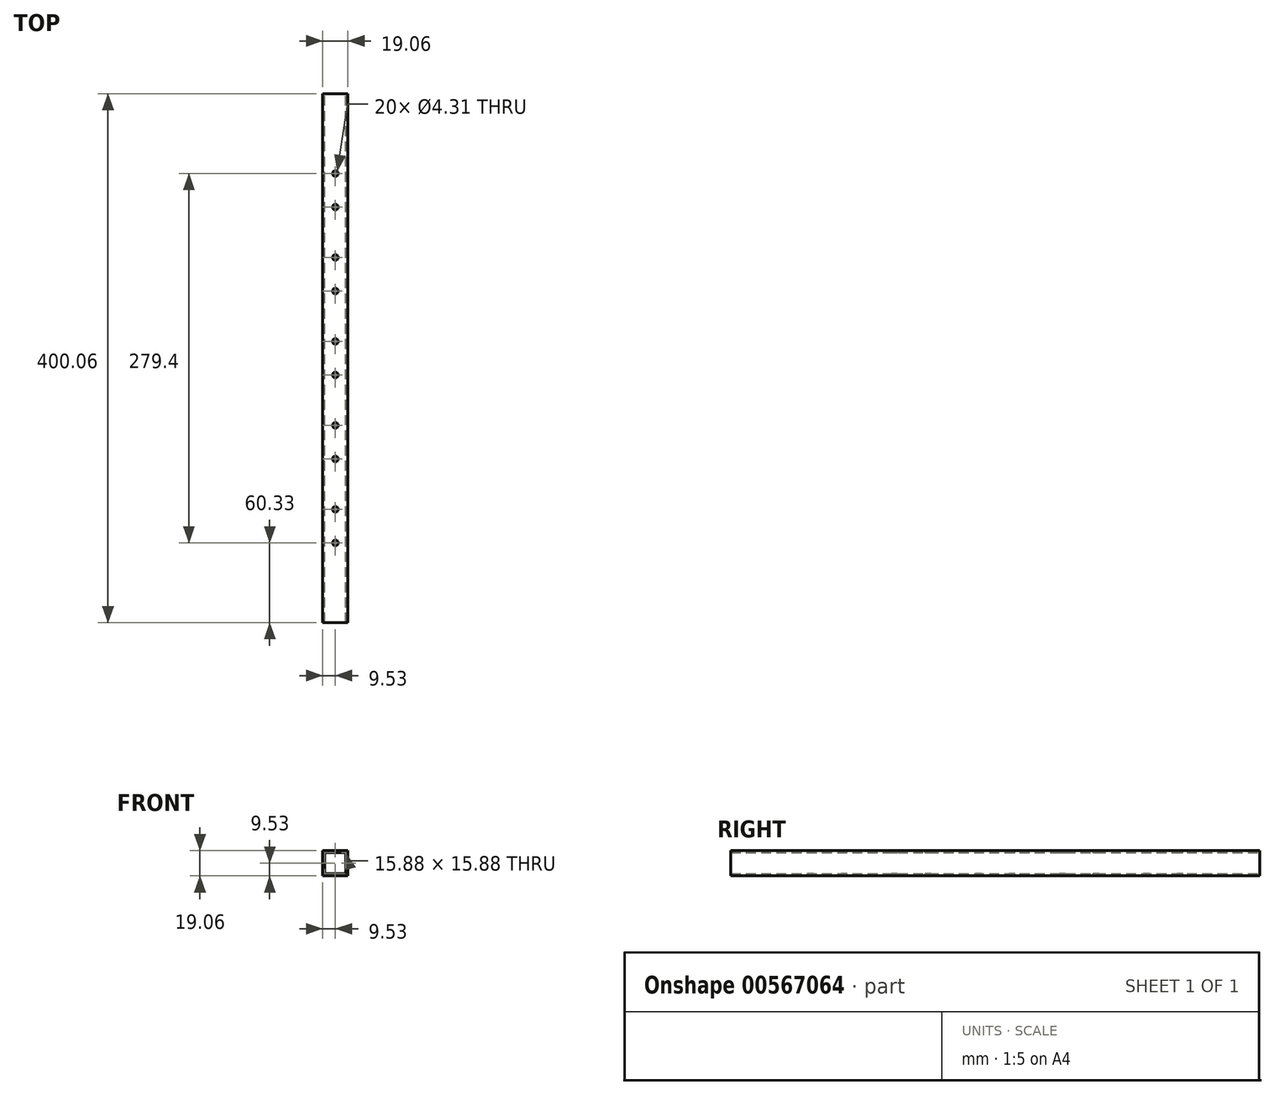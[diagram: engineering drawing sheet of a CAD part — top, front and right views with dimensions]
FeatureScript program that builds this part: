
annotation { "Feature Type Name" : "Feature", "Feature Type Description" : "" }
export const myFeature = defineFeature(function(context is Context, id is Id, definition is map)
    precondition{}
    {
        {
            var Q0;
            Q0=qCreatedBy(makeId("Front.planeOp"),FACE);
            var sketch = newSketch(context, id + "F0", { "sketchPlane" : qUnion([Q0])});
            skLineSegment(sketch, "E0.bottom", {"start": v(-9.52, 9.53) * mm, "end": v(9.53, 9.53) * mm});
            skLineSegment(sketch, "E0.top", {"start": v(-9.53, -9.53) * mm, "end": v(9.52, -9.53) * mm});
            skLineSegment(sketch, "E0.left", {"start": v(-9.52, 9.53) * mm, "end": v(-9.53, -9.52) * mm});
            skLineSegment(sketch, "E0.right", {"start": v(9.53, 9.53) * mm, "end": v(9.52, -9.52) * mm});
            skPoint(sketch, "E0.middle", {"position": v(0, 0) * mm});
            skLineSegment(sketch, "E1.bottom", {"start": v(-7.94, 7.94) * mm, "end": v(7.94, 7.94) * mm});
            skLineSegment(sketch, "E1.top", {"start": v(-7.94, -7.94) * mm, "end": v(7.94, -7.94) * mm});
            skLineSegment(sketch, "E1.left", {"start": v(-7.94, 7.94) * mm, "end": v(-7.94, -7.94) * mm});
            skLineSegment(sketch, "E1.right", {"start": v(7.94, 7.94) * mm, "end": v(7.94, -7.94) * mm});
            skSolve(sketch);
        }
        {
            var Q0;
            Q0=qSketchRegion(id+"F0",true);
            extrude(context, id + "F1", {"entities" : qUnion([Q0]), "endBound" : BoundingType.SYMMETRIC, "depth" : 400.05 * mm, "offsetDistance" : 25.4 * mm});
        }
        {
            var Q0;
            Q0=makeQuery(id+"F1.opExtrude","SWEPT_FACE",FACE,{"disambiguationData":[OSD([sQuery(id+"F0.wireOp",EDGE,"E0.bottom")])]});
            var sketch = newSketch(context, id + "F2", { "sketchPlane" : qUnion([Q0])});
            skCircle(sketch, "E2", {"center": v(0, 12.7) * mm, "radius": 2.15 * mm});
            skCircle(sketch, "E3.MirrorC", {"center": v(0, -12.7) * mm, "radius": 2.15 * mm});
            skCircle(sketch, "E4.0.1.0", {"center": v(0, 76.2) * mm, "radius": 2.15 * mm});
            skCircle(sketch, "E4.0.1.1", {"center": v(0, 50.8) * mm, "radius": 2.15 * mm});
            skCircle(sketch, "E4.0.2.0", {"center": v(0, 139.7) * mm, "radius": 2.15 * mm});
            skCircle(sketch, "E4.0.2.1", {"center": v(0, 114.3) * mm, "radius": 2.15 * mm});
            skLineSegment(sketch, "E4.direction1", {"start": v(0, 12.7) * mm, "end": v(25.4, 12.7) * mm, "construction": true});
            skLineSegment(sketch, "E4.direction2", {"start": v(0, 12.7) * mm, "end": v(0, 76.2) * mm, "construction": true});
            skCircle(sketch, "E5.MirrorC", {"center": v(0, -50.8) * mm, "radius": 2.15 * mm});
            skCircle(sketch, "E6.MirrorC", {"center": v(0, -76.2) * mm, "radius": 2.15 * mm});
            skCircle(sketch, "E7.MirrorC", {"center": v(0, -114.3) * mm, "radius": 2.15 * mm});
            skCircle(sketch, "E8.MirrorC", {"center": v(0, -139.7) * mm, "radius": 2.15 * mm});
            skSolve(sketch);
        }
        {
            var Q0;
            Q0=qSketchRegion(id+"F2",true);
            var Q1;
            Q1=makeQuery(id+"F1.opExtrude","SWEPT_FACE",FACE,{"disambiguationData":[OSD([sQuery(id+"F0.wireOp",EDGE,"E0.top")])]});
            extrude(context, id + "F3", {"entities" : qUnion([Q0, Q1]), "operationType" : NewBodyOperationType.REMOVE, "oppositeDirection" : true, "depth" : 25.4 * mm});
        }
    });
